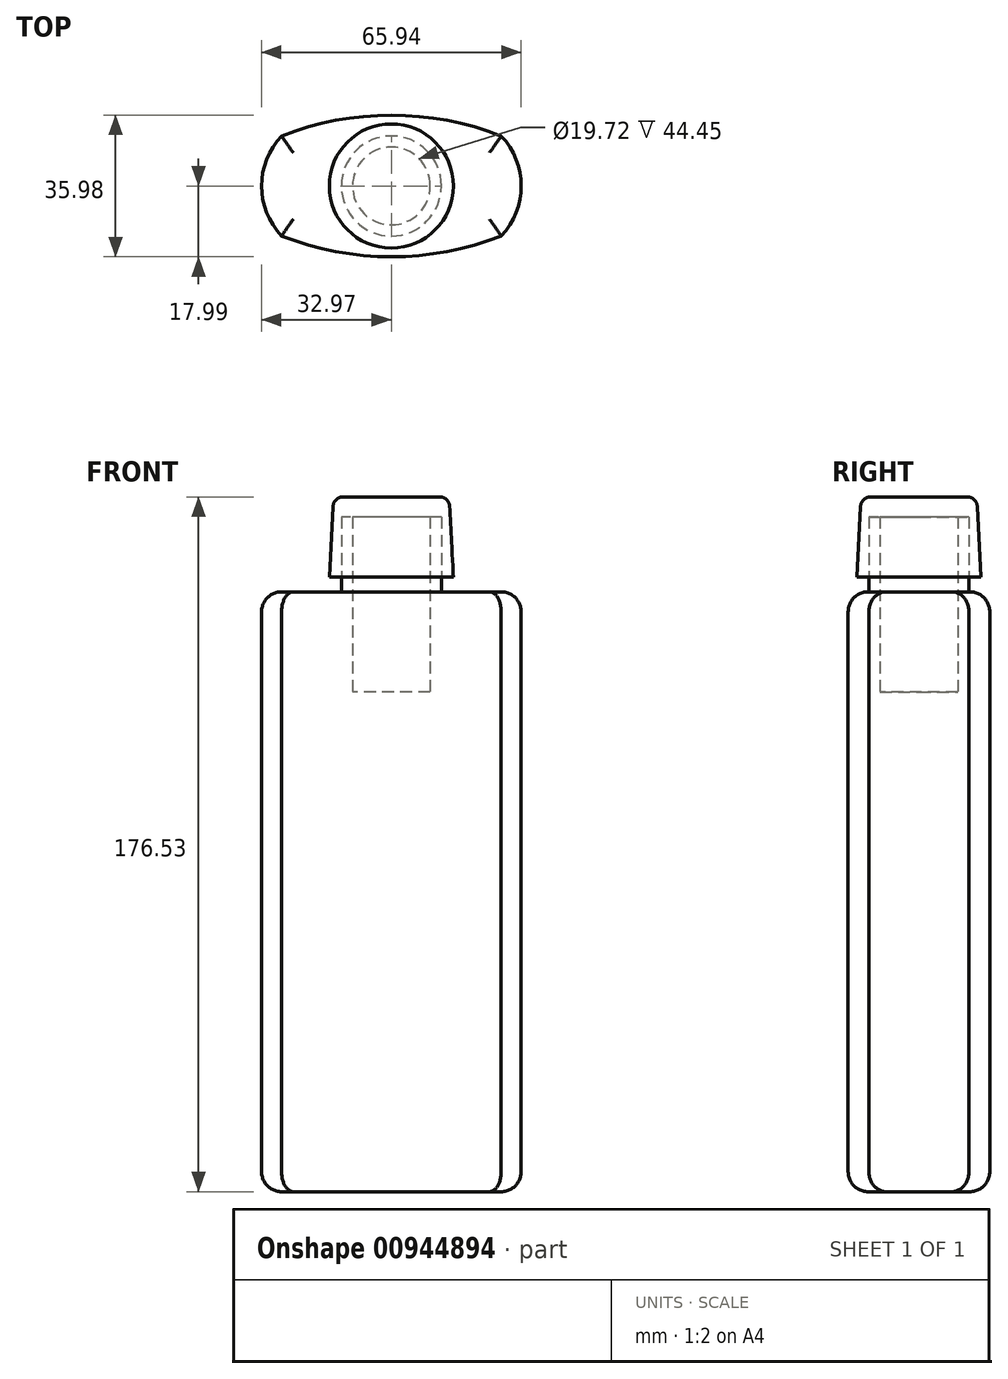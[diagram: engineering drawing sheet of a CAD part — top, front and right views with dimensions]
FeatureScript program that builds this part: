
annotation { "Feature Type Name" : "Feature", "Feature Type Description" : "" }
export const myFeature = defineFeature(function(context is Context, id is Id, definition is map)
    precondition{}
    {
        {
            var Q0;
            Q0=qCreatedBy(makeId("Top.planeOp"),FACE);
            var sketch = newSketch(context, id + "F0", { "sketchPlane" : qUnion([Q0])});
            skArc(sketch, "E0", {"start": v(27.89, 12.7) * mm, "mid": v(0, 17.99) * mm, "end": v(-27.89, 12.7) * mm});
            skArc(sketch, "E1", {"start": v(-27.89, -12.7) * mm, "mid": v(0, -17.99) * mm, "end": v(27.89, -12.7) * mm});
            skArc(sketch, "E2", {"start": v(-27.89, 12.7) * mm, "mid": v(-32.97, 0) * mm, "end": v(-27.89, -12.7) * mm});
            skArc(sketch, "E3", {"start": v(27.89, -12.7) * mm, "mid": v(32.97, 0) * mm, "end": v(27.89, 12.7) * mm});
            skSolve(sketch);
        }
        {
            var Q0;
            Q0=makeQuery(id+"F0.imprint","IMPRINT",FACE,{"disambiguationData":[TD([[makeQuery(id+"F0.imprint","IMPRINT",EDGE,{"derivedFrom":sQuery(id+"F0.wireOp",EDGE,"E0")}),1.0]])]});
            extrude(context, id + "F1", {"entities" : qUnion([Q0]), "depth" : 152.4 * mm, "offsetDistance" : 25.4 * mm});
        }
        {
            var Q0;
            Q0=makeQuery(id+"F1.opExtrude","CAP_FACE",FACE,{"disambiguationData":[OSD([sQuery(id+"F0.wireOp",EDGE,"E0"),sQuery(id+"F0.wireOp",EDGE,"E1"),sQuery(id+"F0.wireOp",EDGE,"E2"),sQuery(id+"F0.wireOp",EDGE,"E3")])],"isStart":false});
            var sketch = newSketch(context, id + "F2", { "sketchPlane" : qUnion([Q0])});
            skCircle(sketch, "E4", {"center": v(0, 0) * mm, "radius": 12.7 * mm});
            skCircle(sketch, "E5", {"center": v(0, 0) * mm, "radius": 9.86 * mm});
            skSolve(sketch);
        }
        {
            var Q0;
            Q0 = qSketchRegion(id + "F2", true);
            extrude(context, id + "F3", {"entities" : qUnion([Q0]), "operationType" : NewBodyOperationType.ADD, "depth" : 19.05 * mm, "offsetDistance" : 25.4 * mm});
        }
        {
            var Q0;
            Q0=makeQuery(id+"F3.boolean.opBoolean","SPLIT",FACE,{"disambiguationData":[TD([makeQuery(id+"F3.opExtrude","SWEPT_FACE",FACE,{"disambiguationData":[OSD([sQuery(id+"F2.wireOp",EDGE,"E5")])]})])],"derivedFrom":makeQuery(id+"F1.opExtrude","CAP_FACE",FACE,{"disambiguationData":[OSD([sQuery(id+"F0.wireOp",EDGE,"E0"),sQuery(id+"F0.wireOp",EDGE,"E1"),sQuery(id+"F0.wireOp",EDGE,"E2"),sQuery(id+"F0.wireOp",EDGE,"E3")])],"isStart":false})});
            extrude(context, id + "F4", {"entities" : qUnion([Q0]), "operationType" : NewBodyOperationType.REMOVE, "oppositeDirection" : true, "depth" : 25.4 * mm, "offsetDistance" : 25.4 * mm});
        }
        {
            var Q0;
            Q0=makeQuery(id+"F3.opExtrude","CAP_FACE",FACE,{"disambiguationData":[OSD([sQuery(id+"F2.wireOp",EDGE,"E4"),sQuery(id+"F2.wireOp",EDGE,"E5")])],"isStart":false});
            var sketch = newSketch(context, id + "F5", { "sketchPlane" : qUnion([Q0])});
            skCircle(sketch, "E6", {"center": v(0, 0) * mm, "radius": 14.97 * mm});
            skSolve(sketch);
        }
        {
            var Q0;
            Q0=makeQuery(id+"F5.imprint","IMPRINT",FACE,{"disambiguationData":[TD([[makeQuery(id+"F5.imprint","IMPRINT",EDGE,{"derivedFrom":sQuery(id+"F5.wireOp",EDGE,"E6")}),1.0]])]});
            var Q1;
            Q1=makeQuery(id+"F5.imprint","IMPRINT",FACE,{"disambiguationData":[TD([[makeQuery(id+"F5.imprint","IMPRINT",EDGE,{"derivedFrom":makeQuery(id+"F3.opExtrude","CAP_EDGE",EDGE,{"disambiguationData":[OSD([sQuery(id+"F2.wireOp",EDGE,"E4")])],"isStart":false})}),1.0]])]});
            var Q2;
            Q2=makeQuery(id+"F5.imprint","IMPRINT",FACE,{"disambiguationData":[TD([[makeQuery(id+"F5.imprint","IMPRINT",EDGE,{"derivedFrom":makeQuery(id+"F3.opExtrude","CAP_EDGE",EDGE,{"disambiguationData":[OSD([sQuery(id+"F2.wireOp",EDGE,"E5")])],"isStart":false})}),1.0]])]});
            var Q3;
            Q3=sQuery(id+"F5.wireOp",EDGE,"E6");
            extrude(context, id + "F6", {"entities" : qUnion([Q0, Q1, Q2]), "surfaceEntities" : qUnion([Q3]), "depth" : 5.08 * mm, "offsetDistance" : 25.4 * mm, "hasDraft" : true, "draftAngle" : 3 * degree, "draftPullDirection" : true, "hasSecondDirection" : true, "secondDirectionOppositeDirection" : true, "secondDirectionDepth" : 15.24 * mm, "hasSecondDirectionDraft" : true, "secondDirectionDraftAngle" : 3 * degree});
        }
        {
            var Q0;
            Q0=makeQuery(id+"F6.opExtrude","CAP_EDGE",EDGE,{"disambiguationData":[OSD([sQuery(id+"F5.wireOp",EDGE,"E6")])],"isStart":false});
            fillet(context, id + "F7", {"entities" : qUnion([Q0]), "radius" : 2.54 * mm, "tangentPropagation" : true, "allowEdgeOverflow" : false});
        }
        {
            var Q0;
            Q0=makeQuery(id+"F1.opExtrude","CAP_EDGE",EDGE,{"disambiguationData":[OSD([sQuery(id+"F0.wireOp",EDGE,"E1")])],"isStart":false});
            var Q1;
            Q1=makeQuery(id+"F1.opExtrude","CAP_EDGE",EDGE,{"disambiguationData":[OSD([sQuery(id+"F0.wireOp",EDGE,"E0")])],"isStart":false});
            var Q2;
            Q2=makeQuery(id+"F1.opExtrude","CAP_EDGE",EDGE,{"disambiguationData":[OSD([sQuery(id+"F0.wireOp",EDGE,"E2")])],"isStart":false});
            var Q3;
            Q3=makeQuery(id+"F1.opExtrude","CAP_EDGE",EDGE,{"disambiguationData":[OSD([sQuery(id+"F0.wireOp",EDGE,"E3")])],"isStart":false});
            var Q4;
            Q4=makeQuery(id+"F1.opExtrude","CAP_EDGE",EDGE,{"disambiguationData":[OSD([sQuery(id+"F0.wireOp",EDGE,"E0")])],"isStart":true});
            var Q5;
            Q5=makeQuery(id+"F1.opExtrude","CAP_EDGE",EDGE,{"disambiguationData":[OSD([sQuery(id+"F0.wireOp",EDGE,"E1")])],"isStart":true});
            var Q6;
            Q6=makeQuery(id+"F1.opExtrude","CAP_EDGE",EDGE,{"disambiguationData":[OSD([sQuery(id+"F0.wireOp",EDGE,"E2")])],"isStart":true});
            var Q7;
            Q7=makeQuery(id+"F1.opExtrude","CAP_EDGE",EDGE,{"disambiguationData":[OSD([sQuery(id+"F0.wireOp",EDGE,"E3")])],"isStart":true});
            fillet(context, id + "F8", {"entities" : qUnion([Q0, Q1, Q2, Q3, Q4, Q5, Q6, Q7]), "radius" : 5.08 * mm, "tangentPropagation" : true, "allowEdgeOverflow" : false});
        }
    });
